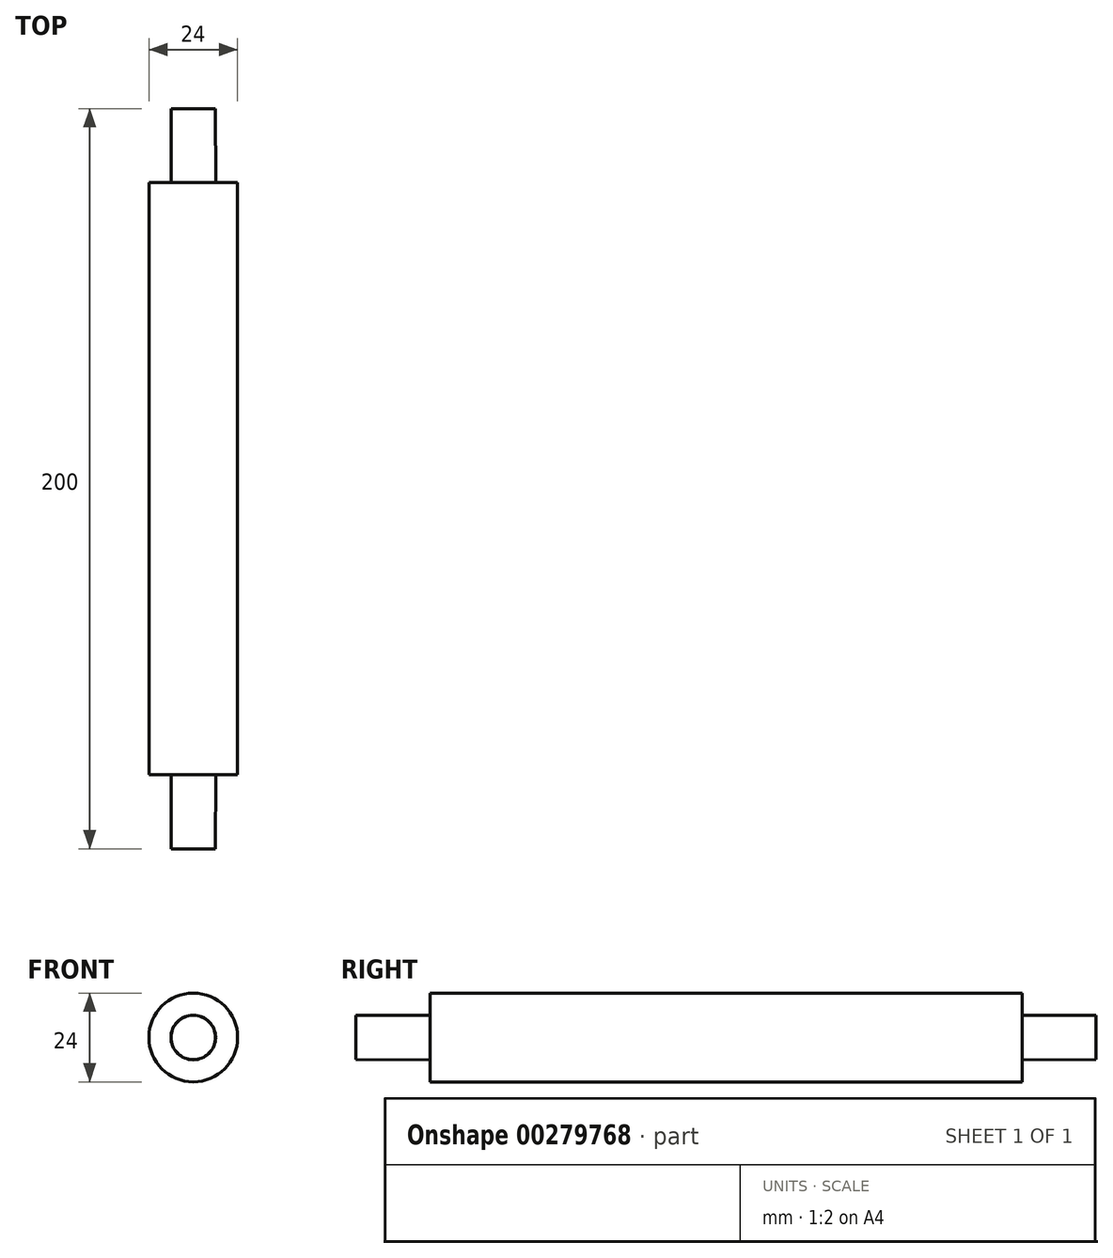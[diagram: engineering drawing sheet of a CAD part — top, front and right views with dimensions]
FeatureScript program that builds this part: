
annotation { "Feature Type Name" : "Feature", "Feature Type Description" : "" }
export const myFeature = defineFeature(function(context is Context, id is Id, definition is map)
    precondition{}
    {
        {
            var Q0;
            Q0=qCreatedBy(makeId("Right.planeOp"),FACE);
            var sketch = newSketch(context, id + "F0", { "sketchPlane" : qUnion([Q0])});
            skLineSegment(sketch, "E0.MirrorCS", {"start": v(100, 6) * mm, "end": v(0, 6.16) * mm});
            skLineSegment(sketch, "E1.MirrorCS", {"start": v(100, 0) * mm, "end": v(100, 6) * mm});
            skLineSegment(sketch, "E2", {"start": v(0, 0) * mm, "end": v(100, 0) * mm});
            skPoint(sketch, "E3.MirrorCS.end.orphan", {"position": v(0, 12) * mm});
            skPoint(sketch, "E3.MirrorCS.start.orphan", {"position": v(80, 12) * mm});
            skPoint(sketch, "E4.MirrorCS.start.orphan", {"position": v(0, 6.16) * mm});
            skPoint(sketch, "E5.end.orphan", {"position": v(-80, 12) * mm});
            skPoint(sketch, "E6.end.orphan", {"position": v(-100, 6) * mm});
            skPoint(sketch, "E7.start.orphan", {"position": v(-100, 0) * mm});
            skLineSegment(sketch, "E8.MirrorCS", {"start": v(-100, 6) * mm, "end": v(0, 6.16) * mm});
            skLineSegment(sketch, "E9.MirrorCS", {"start": v(0, 0) * mm, "end": v(-100, 0) * mm});
            skLineSegment(sketch, "E10.MirrorCS", {"start": v(-100, 0) * mm, "end": v(-100, 6) * mm});
            skLineSegment(sketch, "E11", {"start": v(80, 12) * mm, "end": v(80, 6.03) * mm});
            skLineSegment(sketch, "E12", {"start": v(80, 12) * mm, "end": v(0, 12) * mm});
            skLineSegment(sketch, "E13.MirrorCS", {"start": v(-80, 12) * mm, "end": v(-80, 6.03) * mm});
            skLineSegment(sketch, "E14.MirrorCS", {"start": v(-80, 12) * mm, "end": v(0, 12) * mm});
            skSolve(sketch);
        }
        {
            var Q0;
            Q0=makeQuery(id+"F0.imprint","IMPRINT",FACE,{"disambiguationData":[TD([[makeQuery(id+"F0.imprint","IMPRINT",EDGE,{"derivedFrom":sQuery(id+"F0.wireOp",EDGE,"E0.MirrorCS")}),1.0]])]});
            var Q1;
            Q1=sQuery(id+"F0.wireOp",EDGE,"E9.MirrorCS");
            revolve(context, id + "F1", {"entities" : qUnion([Q0]), "axis" : qUnion([Q1]), "revolveType" : RevolveType.FULL});
        }
        {
            var Q0;
            {var subQ0=sQuery(id+"F0.wireOp",EDGE,"E11");Q0=makeQuery(id+"F0.imprint","IMPRINT",FACE,{"disambiguationData":[TD([[makeQuery(id+"F0.imprint","IMPRINT",EDGE,{"derivedFrom":subQ0}),-1.0]])]});}
            var Q1;
            Q1=sQuery(id+"F0.wireOp",EDGE,"E9.MirrorCS");
            revolve(context, id + "F2", {"operationType" : NewBodyOperationType.ADD, "entities" : qUnion([Q0]), "axis" : qUnion([Q1]), "revolveType" : RevolveType.FULL});
        }
    });
